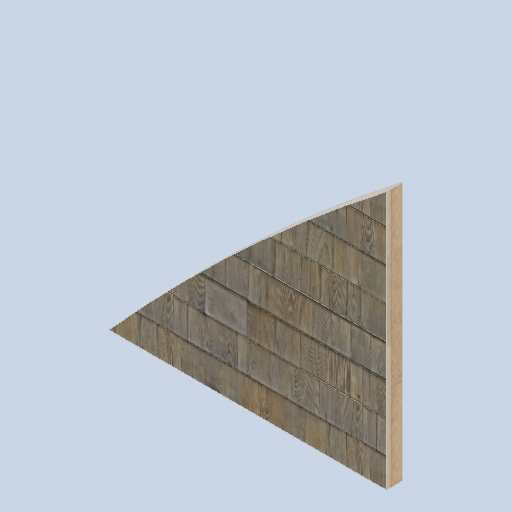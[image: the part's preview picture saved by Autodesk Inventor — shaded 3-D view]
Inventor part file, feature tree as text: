
AUTODESK INVENTOR PART (.ipt)
format: ipt  version: 2024.2 (Build 282272000, 272)  size: 195,584 bytes
history: native  units: in
note: dims shown in document units (in); Inventor stores cm internally (conversion verified against a paired STEP export)
features: other x3, sketch x1
ambient origin geometry x8: Origin, YZ Plane, XZ Plane, XY Plane, X Axis, Y Axis, Z Axis, Center Point
bodies: Solid1 (feature_tree)
feature tree (4):
  other  "front_wall_block01_MIR.ipt"
  other  "Solid1::front_wall_block01_MIR.ipt"
  other  "TaggingFeature1"
  sketch  "Sketch1"  dims[d0=0.3937in]
